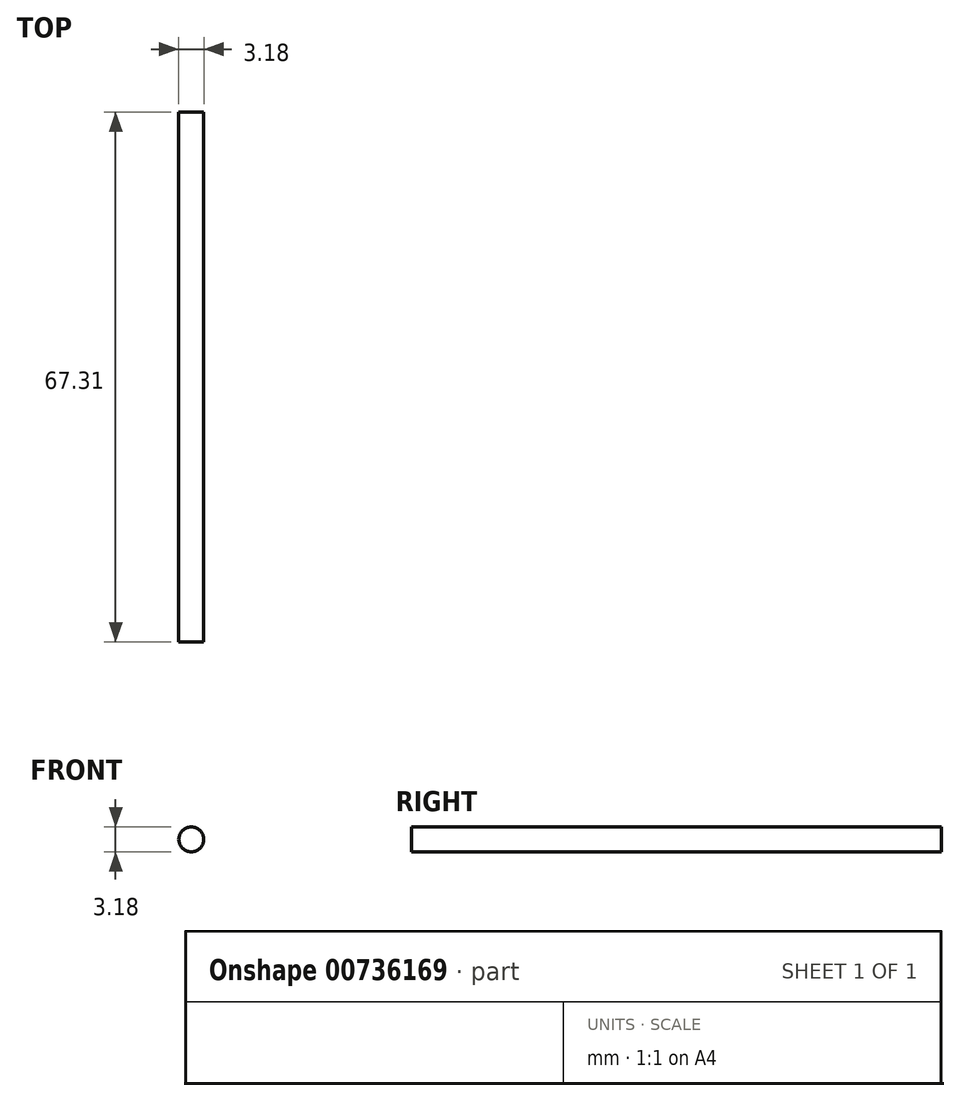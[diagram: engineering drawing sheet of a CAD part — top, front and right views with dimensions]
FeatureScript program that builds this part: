
annotation { "Feature Type Name" : "Feature", "Feature Type Description" : "" }
export const myFeature = defineFeature(function(context is Context, id is Id, definition is map)
    precondition{}
    {
        {
            var Q0;
            Q0=qCreatedBy(makeId("Front.planeOp"),FACE);
            var sketch = newSketch(context, id + "F0", { "sketchPlane" : qUnion([Q0])});
            skCircle(sketch, "E0", {"center": v(0, 0) * mm, "radius": 1.59 * mm});
            skSolve(sketch);
        }
        {
            var Q0;
            Q0=makeQuery(id+"F0.imprint","IMPRINT",FACE,{"disambiguationData":[TD([[makeQuery(id+"F0.imprint","IMPRINT",EDGE,{"derivedFrom":sQuery(id+"F0.wireOp",EDGE,"E0")}),1.0]])]});
            extrude(context, id + "F1", {"entities" : qUnion([Q0]), "depth" : 67.3 * mm, "offsetDistance" : 25.4 * mm});
        }
    });
